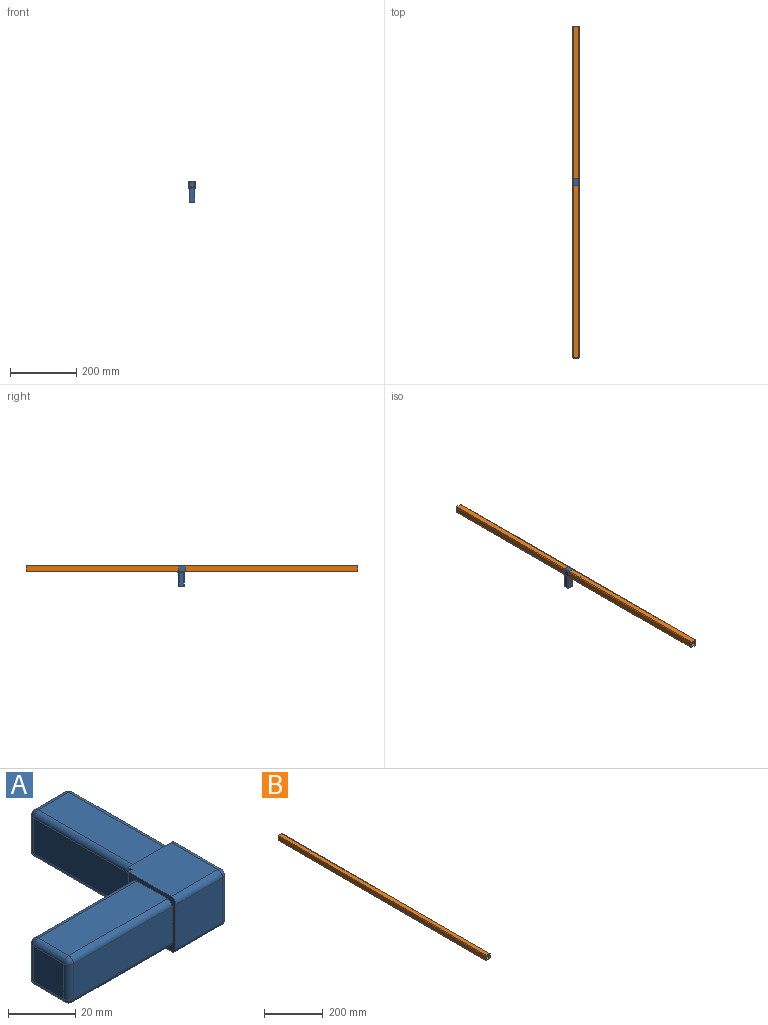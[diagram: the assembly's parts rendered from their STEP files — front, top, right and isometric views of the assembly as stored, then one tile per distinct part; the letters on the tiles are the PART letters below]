
ASSEMBLY  parts=2 mates=4
PART A: 49 faces, bbox 65x65x20 mm
  f0: plane 19.6x19.6mm, normal (0,0,-1), area 381.6mm2, adj f2,f4,f10,f16,f45,f48
  f1: plane 19.6x19.6mm, normal (0,0,1), area 381.6mm2, adj f2,f4,f10,f16,f42,f43
  f2: plane 20x1.6mm, normal (0,1,0), area 32mm2, adj f0,f1,f4,f10
  f3: plane 19.6x16mm, normal (1,0,0), area 313.6mm2, adj f16,f43,f46,f48
  f4: plane 20x1.6mm, normal (-1,0,0), area 32mm2, adj f0,f1,f2,f16
  f5: plane 19.6x16mm, normal (0,-1,0), area 313.6mm2, adj f10,f42,f45,f46
  f6: plane 41.4x12.8mm, normal (0,1,0), area 529.9mm2, adj f10,f35,f39,f41
  f7: plane 41.4x12.8mm, normal (0,0,1), area 529.9mm2, adj f10,f32,f38,f41
  f8: plane 41.4x12.8mm, normal (0,-1,0), area 529.9mm2, adj f10,f30,f32,f33
  f9: plane 41.4x12.8mm, normal (0,0,-1), area 529.9mm2, adj f10,f30,f34,f35
  f10: plane 20x20mm, normal (-1,0,0), area 119.5mm2, adj f0,f1,f2,f5,f6,f7,f8,f9
  f11: plane 12.8x12.8mm, normal (-1,0,0), area 163.8mm2, adj f33,f34,f38,f39
  f12: plane 41.4x12.8mm, normal (1,0,0), area 529.9mm2, adj f16,f23,f27,f29
  f13: plane 41.4x12.8mm, normal (0,0,1), area 529.9mm2, adj f16,f20,f26,f29
  f14: plane 41.4x12.8mm, normal (-1,0,0), area 529.9mm2, adj f16,f18,f20,f21
  f15: plane 41.4x12.8mm, normal (0,0,-1), area 529.9mm2, adj f16,f18,f22,f23
  f16: plane 20x20mm, normal (0,1,0), area 119.5mm2, adj f0,f1,f3,f4,f12,f13,f14,f15
  f17: plane 12.8x12.8mm, normal (0,1,0), area 163.8mm2, adj f21,f22,f26,f27
  f18: cylinder r=2mm len=41.4mm, axis (0,-1,0), area 130.1mm2, adj f14,f15,f16,f19
  f19: sphere r=2mm, area 6.3mm2, adj f18,f21,f22
  f20: cylinder r=2mm len=41.4mm, axis (0,1,0), area 130.1mm2, adj f13,f14,f16,f24
  f21: cylinder r=2mm len=12.8mm, axis (0,0,-1), area 40.2mm2, adj f14,f17,f19,f24
  f22: cylinder r=2mm len=12.8mm, axis (1,0,0), area 40.2mm2, adj f15,f17,f19,f25
  f23: cylinder r=2mm len=41.4mm, axis (0,1,0), area 130.1mm2, adj f12,f15,f16,f25
  f24: sphere r=2mm, area 6.3mm2, adj f20,f21,f26
  f25: sphere r=2mm, area 6.3mm2, adj f22,f23,f27
  f26: cylinder r=2mm len=12.8mm, axis (-1,0,0), area 40.2mm2, adj f13,f17,f24,f28
  f27: cylinder r=2mm len=12.8mm, axis (0,0,1), area 40.2mm2, adj f12,f17,f25,f28
  f28: sphere r=2mm, area 6.3mm2, adj f26,f27,f29
  f29: cylinder r=2mm len=41.4mm, axis (0,-1,0), area 130.1mm2, adj f12,f13,f16,f28
  f30: cylinder r=2mm len=41.4mm, axis (1,0,0), area 130.1mm2, adj f8,f9,f10,f31
  f31: sphere r=2mm, area 6.3mm2, adj f30,f33,f34
  f32: cylinder r=2mm len=41.4mm, axis (-1,0,0), area 130.1mm2, adj f7,f8,f10,f36
  f33: cylinder r=2mm len=12.8mm, axis (0,0,1), area 40.2mm2, adj f8,f11,f31,f36
  f34: cylinder r=2mm len=12.8mm, axis (0,-1,0), area 40.2mm2, adj f9,f11,f31,f37
  f35: cylinder r=2mm len=41.4mm, axis (-1,0,0), area 130.1mm2, adj f6,f9,f10,f37
  f36: sphere r=2mm, area 6.3mm2, adj f32,f33,f38
  f37: sphere r=2mm, area 6.3mm2, adj f34,f35,f39
  f38: cylinder r=2mm len=12.8mm, axis (0,1,0), area 40.2mm2, adj f7,f11,f36,f40
  f39: cylinder r=2mm len=12.8mm, axis (0,0,-1), area 40.2mm2, adj f6,f11,f37,f40
  f40: sphere r=2mm, area 6.3mm2, adj f38,f39,f41
  f41: cylinder r=2mm len=41.4mm, axis (1,0,0), area 130.1mm2, adj f6,f7,f10,f40
  f42: cylinder r=2mm len=19.6mm, axis (1,0,0), area 61.6mm2, adj f1,f5,f10,f44
  f43: cylinder r=2mm len=19.6mm, axis (0,1,0), area 61.6mm2, adj f1,f3,f16,f44
  f44: sphere r=2mm, area 6.3mm2, adj f42,f43,f46
  f45: cylinder r=2mm len=19.6mm, axis (-1,0,0), area 61.6mm2, adj f0,f5,f10,f47
  f46: cylinder r=2mm len=16mm, axis (0,0,-1), area 50.3mm2, adj f3,f5,f44,f47
  f47: sphere r=2mm, area 6.3mm2, adj f45,f46,f48
  f48: cylinder r=2mm len=19.6mm, axis (0,-1,0), area 61.6mm2, adj f0,f3,f16,f47
PART B: 18 faces, bbox 20x1000x20 mm
  f0: plane 1000x16mm, normal (1,0,0), area 16000mm2, adj f1,f15,f16,f17
  f1: cylinder r=2mm len=1000mm, axis (0,1,0), area 3141.6mm2, adj f0,f2,f16,f17
  f2: plane 1000x16mm, normal (0,0,1), area 16000mm2, adj f1,f3,f16,f17
  f3: cylinder r=2mm len=1000mm, axis (0,1,0), area 3141.6mm2, adj f2,f4,f16,f17
  f4: plane 1000x16mm, normal (-1,0,0), area 16000mm2, adj f3,f5,f16,f17
  f5: cylinder r=2mm len=1000mm, axis (0,1,0), area 3141.6mm2, adj f4,f6,f16,f17
  f6: plane 1000x16mm, normal (0,0,-1), area 16000mm2, adj f5,f15,f16,f17
  f7: cylinder r=1mm len=1000mm, axis (0,1,0), area 1570.8mm2, adj f8,f14,f16,f17
  f8: plane 1000x14.81mm, normal (0,0,-1), area 14810.1mm2, adj f7,f9,f16,f17
  f9: cylinder r=1mm len=1000mm, axis (0,1,0), area 1570.8mm2, adj f8,f10,f16,f17
  f10: plane 1000x14.8mm, normal (-1,0,0), area 14800mm2, adj f9,f11,f16,f17
  f11: cylinder r=1mm len=1000mm, axis (0,1,0), area 1570.8mm2, adj f10,f12,f16,f17
  f12: plane 1000x14.81mm, normal (0,0,1), area 14810.1mm2, adj f11,f13,f16,f17
  f13: cylinder r=1mm len=1000mm, axis (0,1,0), area 1570.8mm2, adj f12,f14,f16,f17
  f14: plane 1000x14.8mm, normal (1,0,0), area 14800mm2, adj f7,f13,f16,f17
  f15: cylinder r=2mm len=1000mm, axis (0,1,0), area 3141.6mm2, adj f0,f6,f16,f17
  f16: plane 20x20mm, normal (0,-1,0), area 115mm2, adj f0,f1,f2,f3,f4,f5,f6,f7
  f17: plane 20x20mm, normal (0,1,0), area 115mm2, adj f0,f1,f2,f3,f4,f5,f6,f7
PLACE A rot(axis=(0.71,0,0.71),180deg) t=(-507.02,575.02,168.3)mm
PLACE B t=(-342.56,1097.72,179.33)mm
MATE parallel A.f26 <-> B.f8  axis (0,0,1) through (-500.62,577.02,176.7)mm
MATE slider B.f14 <-> A.f15  axis (1,0,0) through (-515.43,1097.72,175.7)mm
MATE slider A.f14 <-> B.f12  axis (0,0,-1) through (-507.02,597.72,159.9)mm
MATE parallel A.f15 <-> B.f14  axis (-1,0,0) through (-515.42,597.72,168.3)mm
